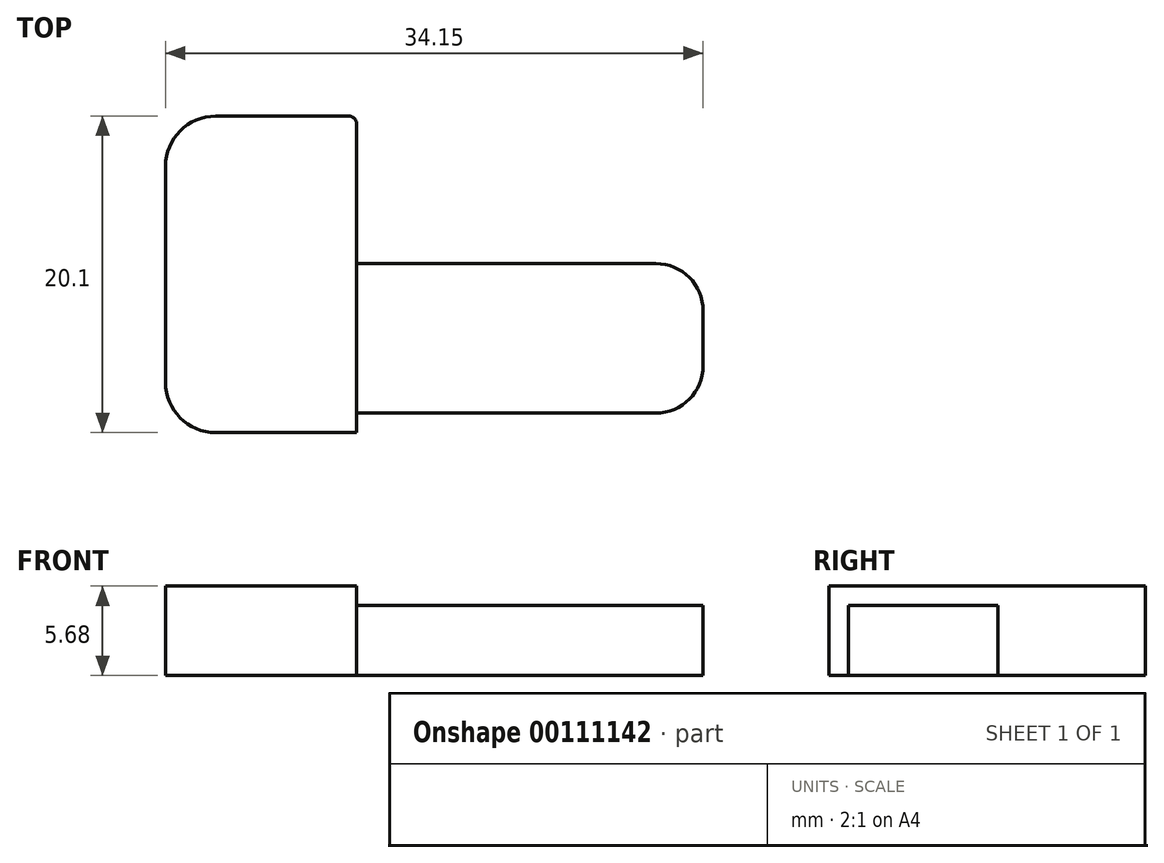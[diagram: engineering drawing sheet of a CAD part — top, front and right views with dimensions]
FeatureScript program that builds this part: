
annotation { "Feature Type Name" : "Feature", "Feature Type Description" : "" }
export const myFeature = defineFeature(function(context is Context, id is Id, definition is map)
    precondition{}
    {
        {
            assignVariable(context, id + "F0", {"name" : "metalWall", "anyValue" : 1.24});
        }
        {
            var Q0;
            Q0=qCreatedBy(makeId("Top.planeOp"),FACE);
            var sketch = newSketch(context, id + "F1", { "sketchPlane" : qUnion([Q0])});
            skLineSegment(sketch, "E0", {"start": v(3.2, 0) * mm, "end": v(12.15, 0) * mm});
            skLineSegment(sketch, "E1", {"start": v(34.15, 0) * mm, "end": v(34.15, 1.24) * mm, "construction": true});
            skLineSegment(sketch, "E2", {"start": v(31.15, 10.73) * mm, "end": v(12.15, 10.73) * mm});
            skLineSegment(sketch, "E3", {"start": v(12.15, 10.73) * mm, "end": v(12.15, 19.6) * mm});
            skLineSegment(sketch, "E4", {"start": v(11.65, 20.1) * mm, "end": v(3.2, 20.1) * mm});
            skLineSegment(sketch, "E5", {"start": v(0, 16.9) * mm, "end": v(0, 3.2) * mm});
            skPoint(sketch, "E6.visualSharp", {"position": v(0, 20.1) * mm});
            skArc(sketch, "E6.filletArc", {"start": v(3.2, 20.1) * mm, "mid": v(0.94, 19.16) * mm, "end": v(0, 16.9) * mm});
            skPoint(sketch, "E7.visualSharp", {"position": v(0, 0) * mm});
            skArc(sketch, "E7.filletArc", {"start": v(0, 3.2) * mm, "mid": v(0.94, 0.94) * mm, "end": v(3.2, 0) * mm});
            skLineSegment(sketch, "E8", {"start": v(31.15, 1.24) * mm, "end": v(12.15, 1.24) * mm});
            skLineSegment(sketch, "E9", {"start": v(12.15, 1.24) * mm, "end": v(12.15, 0) * mm});
            skLineSegment(sketch, "E10", {"start": v(12.15, 11.97) * mm, "end": v(34.15, 11.97) * mm, "construction": true});
            skLineSegment(sketch, "E11", {"start": v(34.15, 11.97) * mm, "end": v(34.15, 10.73) * mm, "construction": true});
            skLineSegment(sketch, "E12", {"start": v(12.15, 0) * mm, "end": v(34.15, 0) * mm, "construction": true});
            skLineSegment(sketch, "E13", {"start": v(34.15, 4.24) * mm, "end": v(34.15, 7.73) * mm});
            skPoint(sketch, "E14.visualSharp", {"position": v(12.15, 20.1) * mm});
            skArc(sketch, "E14.filletArc", {"start": v(12.15, 19.6) * mm, "mid": v(12, 19.95) * mm, "end": v(11.65, 20.1) * mm});
            skLineSegment(sketch, "E15", {"start": v(12.15, 10.73) * mm, "end": v(12.15, 1.24) * mm});
            skPoint(sketch, "E16.visualSharp", {"position": v(34.15, 10.73) * mm});
            skArc(sketch, "E16.filletArc", {"start": v(34.15, 7.73) * mm, "mid": v(33.27, 9.85) * mm, "end": v(31.15, 10.73) * mm});
            skPoint(sketch, "E17.visualSharp", {"position": v(34.15, 1.24) * mm});
            skArc(sketch, "E17.filletArc", {"start": v(31.15, 1.24) * mm, "mid": v(33.27, 2.12) * mm, "end": v(34.15, 4.24) * mm});
            skLineSegment(sketch, "E18", {"start": v(34.15, 1.24) * mm, "end": v(34.15, 4.24) * mm, "construction": true});
            skLineSegment(sketch, "E19", {"start": v(34.15, 1.24) * mm, "end": v(31.15, 1.24) * mm, "construction": true});
            skLineSegment(sketch, "E20", {"start": v(34.15, 7.73) * mm, "end": v(34.15, 10.73) * mm, "construction": true});
            skSolve(sketch);
        }
        {
            var Q0;
            Q0=makeQuery(id+"F1.imprint","IMPRINT",FACE,{"disambiguationData":[TD([[makeQuery(id+"F1.imprint","IMPRINT",EDGE,{"derivedFrom":sQuery(id+"F1.wireOp",EDGE,"E0")}),1.0]])]});
            extrude(context, id + "F2", {"entities" : qUnion([Q0]), "depth" : (6.3 - (getVariable(context, 'metalWall') / 2)) * mm, "offsetDistance" : 25 * mm});
        }
        {
            var Q0;
            Q0=makeQuery(id+"F1.imprint","IMPRINT",FACE,{"disambiguationData":[TD([[makeQuery(id+"F1.imprint","IMPRINT",EDGE,{"derivedFrom":sQuery(id+"F1.wireOp",EDGE,"E2")}),1.0]])]});
            extrude(context, id + "F3", {"entities" : qUnion([Q0]), "operationType" : NewBodyOperationType.ADD, "depth" : (6.3 - (getVariable(context, 'metalWall') + getVariable(context, 'metalWall') / 2)) * mm, "offsetDistance" : 25 * mm});
        }
    });
